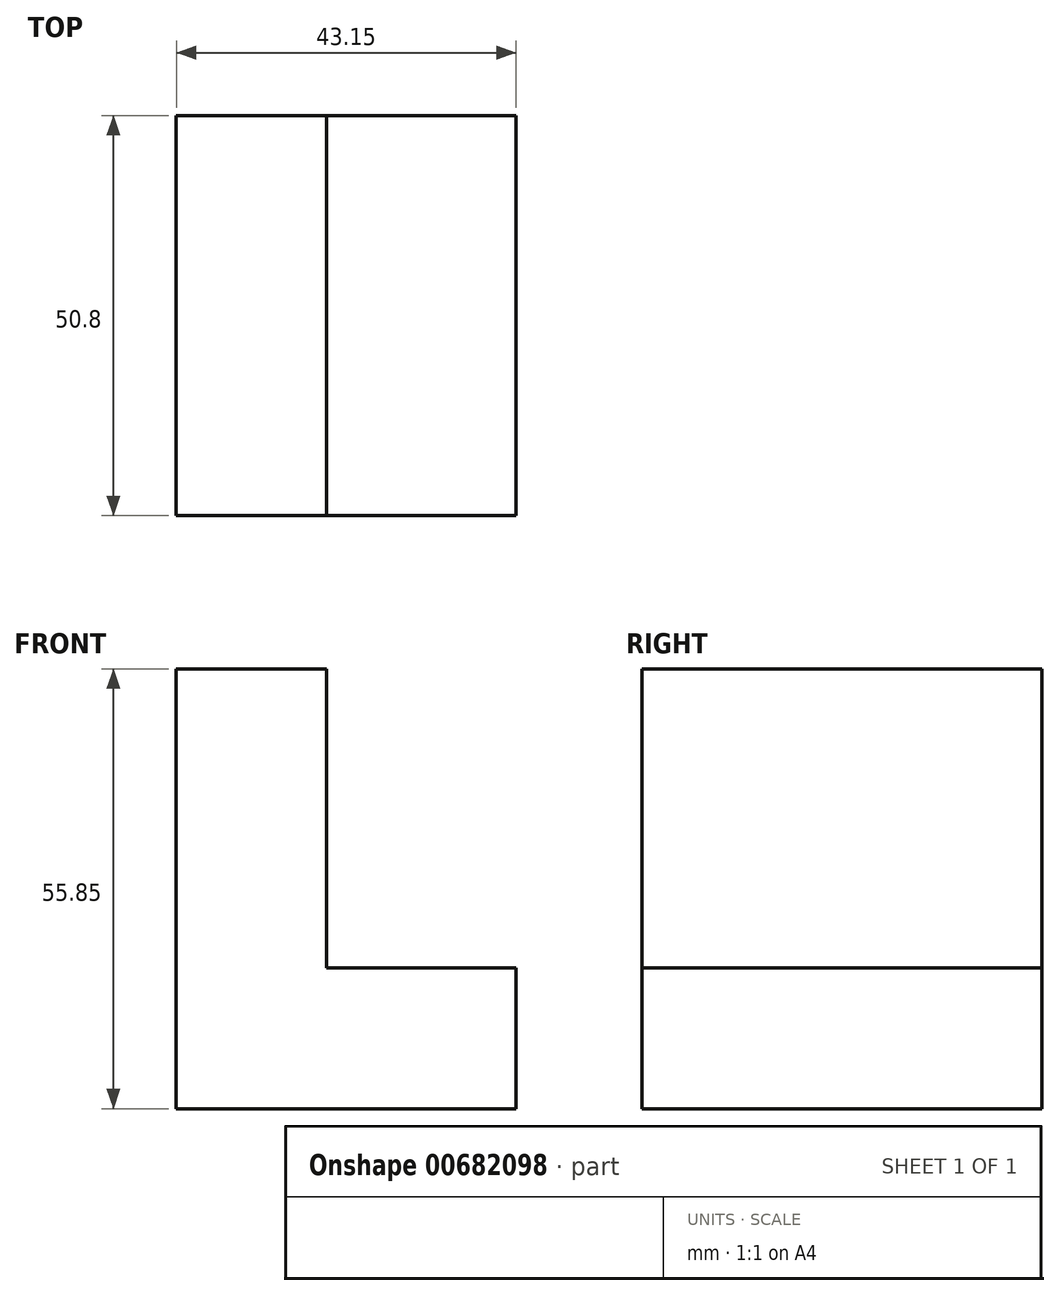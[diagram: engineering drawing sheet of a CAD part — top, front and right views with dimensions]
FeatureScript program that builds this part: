
annotation { "Feature Type Name" : "Feature", "Feature Type Description" : "" }
export const myFeature = defineFeature(function(context is Context, id is Id, definition is map)
    precondition{}
    {
        {
            var Q0;
            Q0=qCreatedBy(makeId("Front.planeOp"),FACE);
            var sketch = newSketch(context, id + "F0", { "sketchPlane" : qUnion([Q0])});
            skLineSegment(sketch, "E0", {"start": v(-71.51, 55.85) * mm, "end": v(-71.51, 0) * mm});
            skLineSegment(sketch, "E1", {"start": v(-71.51, 0) * mm, "end": v(-28.36, 0) * mm});
            skLineSegment(sketch, "E2", {"start": v(-28.36, 0) * mm, "end": v(-28.36, 17.85) * mm});
            skLineSegment(sketch, "E3", {"start": v(-28.36, 17.85) * mm, "end": v(-52.42, 17.85) * mm});
            skLineSegment(sketch, "E4", {"start": v(-52.42, 17.85) * mm, "end": v(-52.42, 55.85) * mm});
            skLineSegment(sketch, "E5", {"start": v(-52.42, 55.85) * mm, "end": v(-71.51, 55.85) * mm});
            skSolve(sketch);
        }
        {
            var Q0;
            Q0 = qSketchRegion(id + "F0", true);
            extrude(context, id + "F1", {"entities" : qUnion([Q0]), "depth" : 50.8 * mm, "offsetDistance" : 25.4 * mm});
        }
    });
